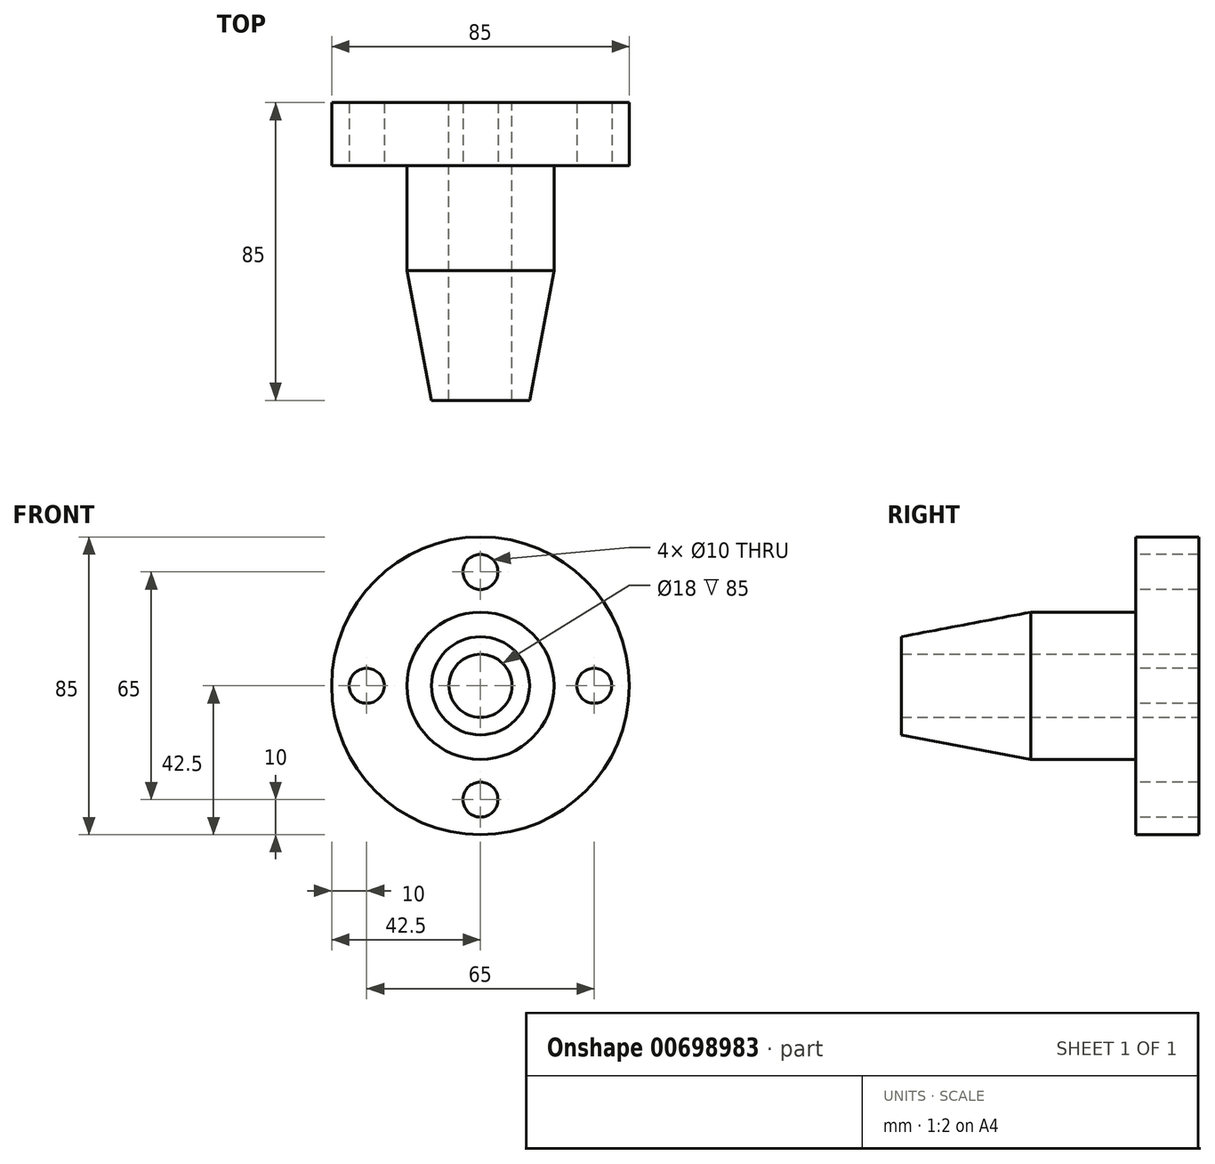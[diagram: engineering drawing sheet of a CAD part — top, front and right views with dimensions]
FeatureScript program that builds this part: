
annotation { "Feature Type Name" : "Feature", "Feature Type Description" : "" }
export const myFeature = defineFeature(function(context is Context, id is Id, definition is map)
    precondition{}
    {
        {
            var Q0;
            Q0=qCreatedBy(makeId("Top.planeOp"),FACE);
            var sketch = newSketch(context, id + "F0", { "sketchPlane" : qUnion([Q0])});
            skLineSegment(sketch, "E0", {"start": v(0, 46.14) * mm, "end": v(0, -46.14) * mm, "construction": true});
            skLineSegment(sketch, "E1", {"start": v(9, -42.5) * mm, "end": v(9, 42.5) * mm});
            skLineSegment(sketch, "E2", {"start": v(9, 42.5) * mm, "end": v(42.5, 42.5) * mm});
            skLineSegment(sketch, "E3", {"start": v(42.5, 42.5) * mm, "end": v(42.5, 24.5) * mm});
            skLineSegment(sketch, "E4", {"start": v(42.5, 24.5) * mm, "end": v(21, 24.5) * mm});
            skLineSegment(sketch, "E5", {"start": v(21, 24.5) * mm, "end": v(21, -5.5) * mm});
            skLineSegment(sketch, "E6", {"start": v(21, -5.5) * mm, "end": v(14, -42.5) * mm});
            skLineSegment(sketch, "E7", {"start": v(14, -42.5) * mm, "end": v(9, -42.5) * mm});
            skSolve(sketch);
        }
        {
            var Q0;
            Q0=makeQuery(id+"F0.imprint","IMPRINT",FACE,{"disambiguationData":[TD([[makeQuery(id+"F0.imprint","IMPRINT",EDGE,{"derivedFrom":sQuery(id+"F0.wireOp",EDGE,"E1")}),-1.0]])]});
            var Q1;
            Q1=sQuery(id+"F0.wireOp",EDGE,"E0");
            revolve(context, id + "F1", {"entities" : qUnion([Q0]), "axis" : qUnion([Q1]), "revolveType" : RevolveType.FULL});
        }
        {
            var Q0;
            Q0=makeQuery(id+"F1.opRevolve","SWEPT_FACE",FACE,{"disambiguationData":[OSD([sQuery(id+"F0.wireOp",EDGE,"E4")])]});
            var sketch = newSketch(context, id + "F2", { "sketchPlane" : qUnion([Q0])});
            skLineSegment(sketch, "E8", {"start": v(0, 0) * mm, "end": v(0, 32.5) * mm});
            skLineSegment(sketch, "E9", {"start": v(0, 0) * mm, "end": v(32.5, 0) * mm});
            skLineSegment(sketch, "E10", {"start": v(0, 0) * mm, "end": v(0, -32.5) * mm});
            skLineSegment(sketch, "E11", {"start": v(0, 0) * mm, "end": v(-32.5, 0) * mm});
            skSolve(sketch);
        }
        {
            var Q0;
            Q0=sQuery(id+"F2.wireOp",VERTEX,"E8.end");
            var Q1;
            Q1=sQuery(id+"F2.wireOp",VERTEX,"E9.end");
            var Q2;
            Q2=sQuery(id+"F2.wireOp",VERTEX,"E10.end");
            var Q3;
            Q3=sQuery(id+"F2.wireOp",VERTEX,"E11.end");
            var Q4;
            Q4=makeQuery(id+"F1.opRevolve","SWEPT_BODY",BODY,{"disambiguationData":[OSD([sQuery(id+"F0.wireOp",EDGE,"E1"),sQuery(id+"F0.wireOp",EDGE,"E2"),sQuery(id+"F0.wireOp",EDGE,"E3"),sQuery(id+"F0.wireOp",EDGE,"E4"),sQuery(id+"F0.wireOp",EDGE,"E5"),sQuery(id+"F0.wireOp",EDGE,"E6"),sQuery(id+"F0.wireOp",EDGE,"E7")])]});
            hole(context, id + "F3", {"style" : HoleStyle.SIMPLE, "endStyle" : HoleEndStyle.THROUGH, "holeDiameter" : 10 * mm, "majorDiameter" : 5 * mm, "isTappedThrough" : true, "tappedDepth" : 12 * mm, "tapClearance" : 3, "locations" : qUnion([Q0, Q1, Q2, Q3]), "scope" : qUnion([Q4])});
        }
    });
